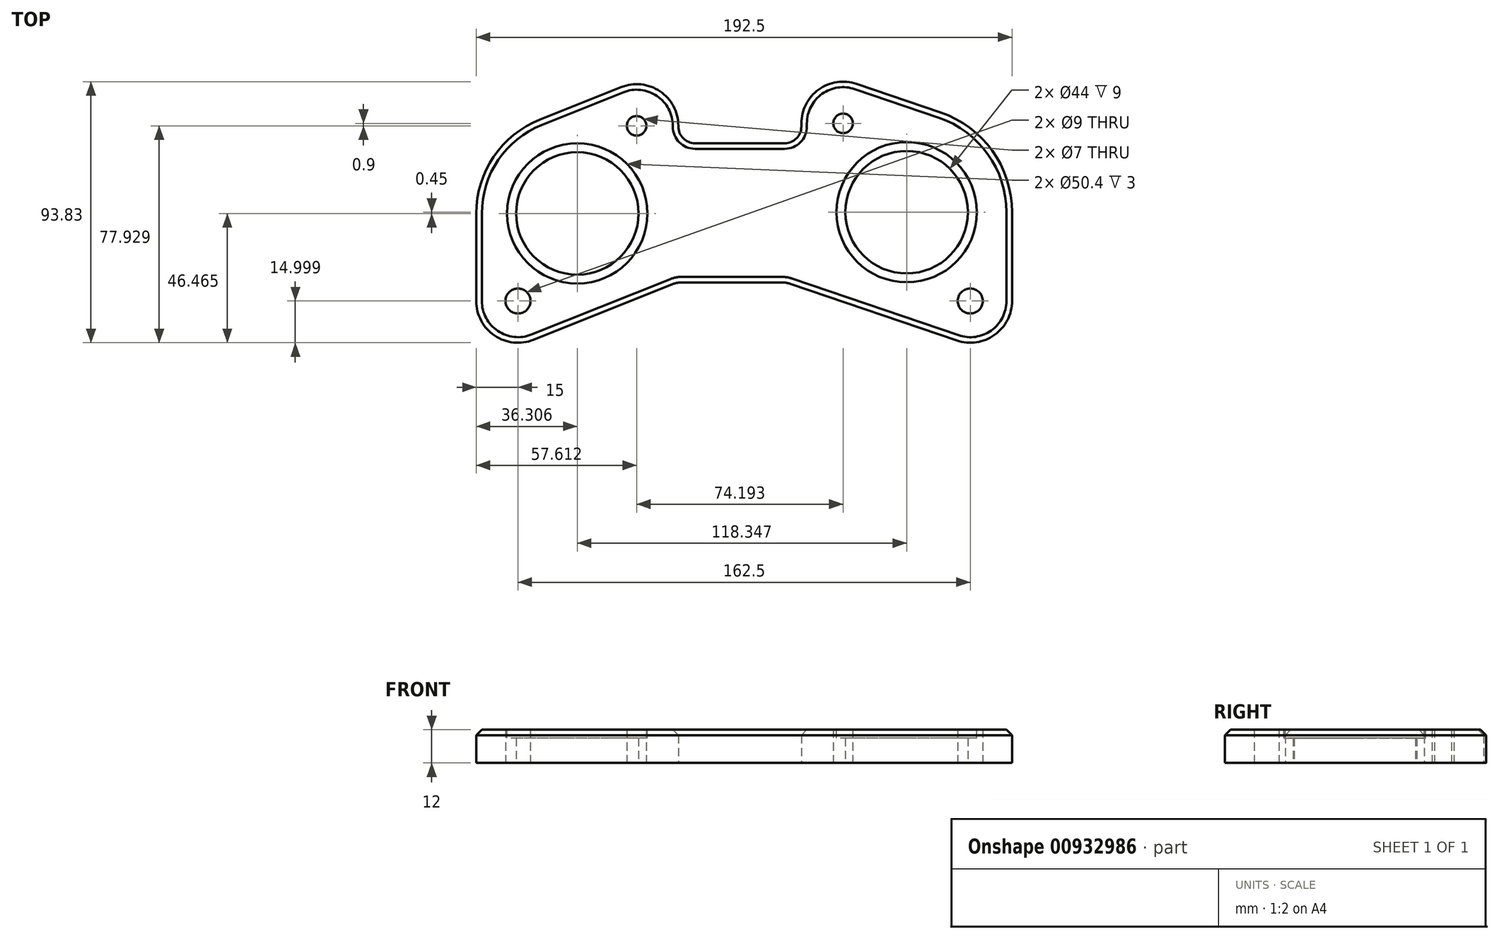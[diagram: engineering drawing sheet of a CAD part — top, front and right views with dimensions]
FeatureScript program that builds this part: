
annotation { "Feature Type Name" : "Feature", "Feature Type Description" : "" }
export const myFeature = defineFeature(function(context is Context, id is Id, definition is map)
    precondition{}
    {
        {
            var Q0;
            Q0=qCreatedBy(makeId("Top.planeOp"),FACE);
            var sketch = newSketch(context, id + "F0", { "sketchPlane" : qUnion([Q0])});
            skCircle(sketch, "E0", {"center": v(81.25, -39.3) * mm, "radius": 4.5 * mm});
            skCircle(sketch, "E1", {"center": v(-81.25, -39.3) * mm, "radius": 4.5 * mm});
            skCircle(sketch, "E2", {"center": v(-38.64, 23.63) * mm, "radius": 3.5 * mm});
            skCircle(sketch, "E3", {"center": v(35.56, 24.53) * mm, "radius": 3.5 * mm});
            skCircle(sketch, "E4", {"center": v(-59.94, -7.84) * mm, "radius": 22 * mm});
            skCircle(sketch, "E5", {"center": v(58.4, -7.39) * mm, "radius": 22 * mm});
            skArc(sketch, "E6", {"start": v(-96.25, -39.3) * mm, "mid": v(-89.66, -51.72) * mm, "end": v(-75.68, -53.23) * mm});
            skArc(sketch, "E7", {"start": v(76.42, -53.5) * mm, "mid": v(89.98, -51.5) * mm, "end": v(96.25, -39.3) * mm});
            skArc(sketch, "E8", {"start": v(40.4, 38.73) * mm, "mid": v(26.82, 36.73) * mm, "end": v(20.56, 24.53) * mm});
            skArc(sketch, "E9", {"start": v(-23.64, 23.63) * mm, "mid": v(-30.23, 36.05) * mm, "end": v(-44.2, 37.56) * mm});
            skArc(sketch, "E10", {"start": v(96.25, -7.39) * mm, "mid": v(89.18, 14.65) * mm, "end": v(70.6, 28.44) * mm});
            skArc(sketch, "E11", {"start": v(-73.42, 25.88) * mm, "mid": v(-90, 12.52) * mm, "end": v(-96.25, -7.84) * mm});
            skLineSegment(sketch, "E12", {"start": v(-44.2, 37.56) * mm, "end": v(-73.42, 25.88) * mm});
            skLineSegment(sketch, "E13", {"start": v(-96.25, -7.84) * mm, "end": v(-96.25, -39.3) * mm});
            skLineSegment(sketch, "E14", {"start": v(70.6, 28.44) * mm, "end": v(40.4, 38.73) * mm});
            skLineSegment(sketch, "E15", {"start": v(96.25, -39.3) * mm, "end": v(96.25, -7.39) * mm});
            skLineSegment(sketch, "E16", {"start": v(-75.68, -53.23) * mm, "end": v(-25.9, -33.33) * mm});
            skArc(sketch, "E17", {"start": v(-25.9, -33.33) * mm, "mid": v(-24.08, -32.8) * mm, "end": v(-22.19, -32.61) * mm});
            skLineSegment(sketch, "E18", {"start": v(-22.19, -32.61) * mm, "end": v(13.41, -32.61) * mm});
            skArc(sketch, "E19", {"start": v(13.41, -32.61) * mm, "mid": v(15.04, -32.74) * mm, "end": v(16.63, -33.14) * mm});
            skLineSegment(sketch, "E20", {"start": v(16.63, -33.14) * mm, "end": v(76.42, -53.5) * mm});
            skLineSegment(sketch, "E21", {"start": v(20.56, 24.53) * mm, "end": v(20.56, 23.39) * mm});
            skArc(sketch, "E22", {"start": v(20.56, 23.39) * mm, "mid": v(18.8, 19.15) * mm, "end": v(14.56, 17.39) * mm});
            skLineSegment(sketch, "E23", {"start": v(14.56, 17.39) * mm, "end": v(-17.64, 17.39) * mm});
            skArc(sketch, "E24", {"start": v(-17.64, 17.39) * mm, "mid": v(-21.88, 19.15) * mm, "end": v(-23.64, 23.39) * mm});
            skLineSegment(sketch, "E25", {"start": v(-23.64, 23.39) * mm, "end": v(-23.64, 23.63) * mm});
            skSolve(sketch);
        }
        {
            var Q0;
            Q0=qSketchRegion(id+"F0",true);
            extrude(context, id + "F1", {"entities" : qUnion([Q0]), "depth" : 12 * mm, "offsetDistance" : 25 * mm});
        }
        {
            var Q0;
            Q0=makeQuery(id+"F1.opExtrude","CAP_FACE",FACE,{"disambiguationData":[OSD([sQuery(id+"F0.wireOp",EDGE,"E0"),sQuery(id+"F0.wireOp",EDGE,"E1"),sQuery(id+"F0.wireOp",EDGE,"E2"),sQuery(id+"F0.wireOp",EDGE,"E3"),sQuery(id+"F0.wireOp",EDGE,"E4"),sQuery(id+"F0.wireOp",EDGE,"E5"),sQuery(id+"F0.wireOp",EDGE,"E6"),sQuery(id+"F0.wireOp",EDGE,"E7"),sQuery(id+"F0.wireOp",EDGE,"E8"),sQuery(id+"F0.wireOp",EDGE,"E9"),sQuery(id+"F0.wireOp",EDGE,"E10"),sQuery(id+"F0.wireOp",EDGE,"E11"),sQuery(id+"F0.wireOp",EDGE,"E12"),sQuery(id+"F0.wireOp",EDGE,"E13"),sQuery(id+"F0.wireOp",EDGE,"E14"),sQuery(id+"F0.wireOp",EDGE,"E15"),sQuery(id+"F0.wireOp",EDGE,"E16"),sQuery(id+"F0.wireOp",EDGE,"E17"),sQuery(id+"F0.wireOp",EDGE,"E18"),sQuery(id+"F0.wireOp",EDGE,"E19"),sQuery(id+"F0.wireOp",EDGE,"E20"),sQuery(id+"F0.wireOp",EDGE,"E21"),sQuery(id+"F0.wireOp",EDGE,"E22"),sQuery(id+"F0.wireOp",EDGE,"E23"),sQuery(id+"F0.wireOp",EDGE,"E24"),sQuery(id+"F0.wireOp",EDGE,"E25")])],"isStart":false});
            var sketch = newSketch(context, id + "F2", { "sketchPlane" : qUnion([Q0])});
            skCircle(sketch, "E26.0", {"center": v(-59.94, -7.84) * mm, "radius": 25.2 * mm});
            skCircle(sketch, "E27.0", {"center": v(58.4, -7.39) * mm, "radius": 25.2 * mm});
            skSolve(sketch);
        }
        {
            var Q0;
            Q0=qSketchRegion(id+"F2",true);
            extrude(context, id + "F3", {"entities" : qUnion([Q0]), "operationType" : NewBodyOperationType.REMOVE, "oppositeDirection" : true, "depth" : 3 * mm, "offsetDistance" : 25 * mm});
        }
        {
            var Q0;
            Q0=makeQuery(id+"F1.opExtrude","CAP_EDGE",EDGE,{"disambiguationData":[OSD([sQuery(id+"F0.wireOp",EDGE,"E12")])],"isStart":false});
            chamfer(context, id + "F4", {"entities" : qUnion([Q0]), "width" : 2 * mm, "tangentPropagation" : true});
        }
    });
